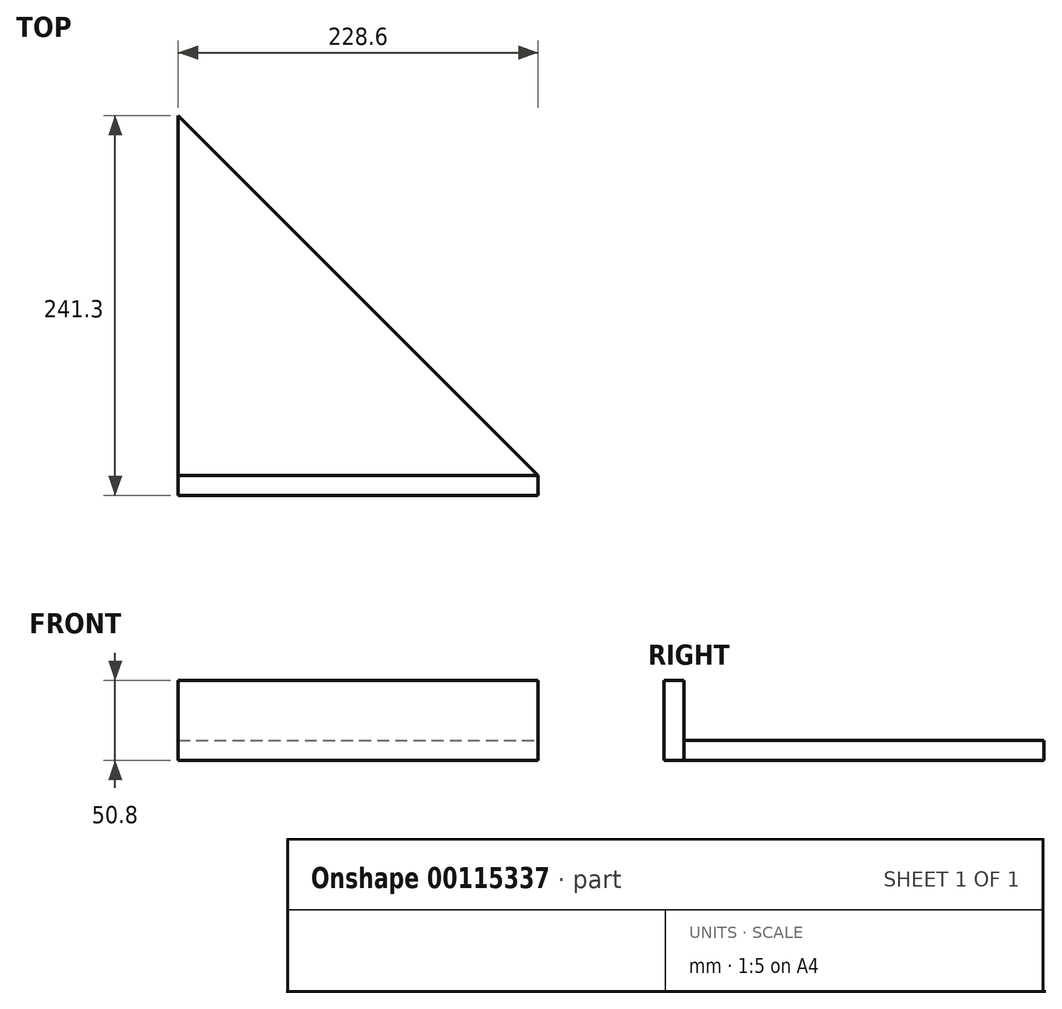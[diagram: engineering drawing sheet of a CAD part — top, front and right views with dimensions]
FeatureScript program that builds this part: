
annotation { "Feature Type Name" : "Feature", "Feature Type Description" : "" }
export const myFeature = defineFeature(function(context is Context, id is Id, definition is map)
    precondition{}
    {
        {
            var Q0;
            Q0=qCreatedBy(makeId("Front.planeOp"),FACE);
            var sketch = newSketch(context, id + "F0", { "sketchPlane" : qUnion([Q0])});
            skLineSegment(sketch, "E0.bottom", {"start": v(-114.3, 25.4) * mm, "end": v(114.3, 25.4) * mm});
            skLineSegment(sketch, "E0.top", {"start": v(-114.3, -25.4) * mm, "end": v(114.3, -25.4) * mm});
            skLineSegment(sketch, "E0.left", {"start": v(-114.3, 25.4) * mm, "end": v(-114.3, -25.4) * mm});
            skLineSegment(sketch, "E0.right", {"start": v(114.3, 25.4) * mm, "end": v(114.3, -25.4) * mm});
            skPoint(sketch, "E0.middle", {"position": v(0, 0) * mm});
            skSolve(sketch);
        }
        {
            var Q0;
            Q0=makeQuery(id+"F0.imprint","IMPRINT",FACE,{"disambiguationData":[TD([[makeQuery(id+"F0.imprint","IMPRINT",EDGE,{"derivedFrom":sQuery(id+"F0.wireOp",EDGE,"E0.bottom")}),-1.0]])]});
            extrude(context, id + "F1", {"entities" : qUnion([Q0]), "depth" : 12.7 * mm});
        }
        {
            var Q0;
            Q0=makeQuery(id+"F1.opExtrude","CAP_FACE",FACE,{"disambiguationData":[OSD([sQuery(id+"F0.wireOp",EDGE,"E0.bottom"),sQuery(id+"F0.wireOp",EDGE,"E0.top"),sQuery(id+"F0.wireOp",EDGE,"E0.left"),sQuery(id+"F0.wireOp",EDGE,"E0.right")])],"isStart":true});
            var sketch = newSketch(context, id + "F2", { "sketchPlane" : qUnion([Q0])});
            skLineSegment(sketch, "E1.bottom", {"start": v(114.3, -25.4) * mm, "end": v(-114.3, -25.4) * mm});
            skLineSegment(sketch, "E1.top", {"start": v(114.3, -12.7) * mm, "end": v(-114.3, -12.7) * mm});
            skLineSegment(sketch, "E1.left", {"start": v(114.3, -25.4) * mm, "end": v(114.3, -12.7) * mm});
            skLineSegment(sketch, "E1.right", {"start": v(-114.3, -25.4) * mm, "end": v(-114.3, -12.7) * mm});
            skSolve(sketch);
        }
        {
            var Q0;
            Q0 = qSketchRegion(id + "F2", true);
            extrude(context, id + "F3", {"entities" : qUnion([Q0]), "operationType" : NewBodyOperationType.ADD, "depth" : 228.6 * mm});
        }
        {
            var Q0;
            Q0=makeQuery(id+"F3.opExtrude","SWEPT_FACE",FACE,{"disambiguationData":[OSD([sQuery(id+"F2.wireOp",EDGE,"E1.top")])]});
            var sketch = newSketch(context, id + "F4", { "sketchPlane" : qUnion([Q0])});
            skLineSegment(sketch, "E2", {"start": v(-114.3, 228.6) * mm, "end": v(114.3, 0) * mm});
            skLineSegment(sketch, "E3", {"start": v(114.3, 0) * mm, "end": v(114.3, 228.6) * mm});
            skLineSegment(sketch, "E4", {"start": v(114.3, 228.6) * mm, "end": v(-114.3, 228.6) * mm});
            skSolve(sketch);
        }
        {
            var Q0;
            Q0 = qSketchRegion(id + "F4", true);
            extrude(context, id + "F5", {"entities" : qUnion([Q0]), "operationType" : NewBodyOperationType.REMOVE, "oppositeDirection" : true, "depth" : 25.4 * mm});
        }
    });
